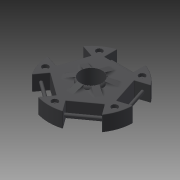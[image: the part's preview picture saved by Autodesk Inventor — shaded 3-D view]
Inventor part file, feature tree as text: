
AUTODESK INVENTOR PART (.ipt)
format: ipt  version: 2014 SP2 (Build 180246200, 246)  size: 1,258,496 bytes
history: native  units: mm
features: extrude x11, sketch x11, fillet x6, projected_geometry x3, pattern_circular x2
ambient origin geometry x8: Origin, YZ Plane, XZ Plane, XY Plane, X Axis, Y Axis, Z Axis, Center Point
bodies: Solid1 (feature_tree)
feature tree (33):
  extrude  "Extrusion1"  Depth=10.0mm TaperAngle=0.0deg
  extrude  "Extrusion2"  Depth=10.0mm TaperAngle=0.0deg
  extrude  "Extrusion3"  Depth=50.0mm TaperAngle=360.0deg
  extrude  "Extrusion4"  Depth=20.0mm TaperAngle=0.0deg
  pattern_circular  "Circular Pattern1"  Count=5 Angle=360.0deg
  extrude  "Extrusion5"  Depth=2.0mm TaperAngle=360.0deg
  extrude  "Extrusion6"  Depth=0.3mm
  extrude  "Extrusion7"  Depth=2.0mm
  fillet  "Fillet1"  Radius=2.5mm
  extrude  "Extrusion8"  Depth=2.0mm TaperAngle=0.0deg
  fillet  "Fillet2"  Radius=5.0mm
  fillet  "Fillet3"  Radius=2.0mm
  extrude  "Extrusion9"  Depth=2.0mm TaperAngle=360.0deg
  extrude  "Extrusion10"  [1 undecoded]
  fillet  "Fillet4"  [1 undecoded]
  fillet  "Fillet5"  [1 undecoded]
  fillet  "Fillet6"  [1 undecoded]
  pattern_circular  "Circular Pattern2"  [2 undecoded]
  extrude  "Extrusion11"  [1 undecoded]
  sketch  "Sketch1"  dims[d1=10.0mm d2=0.0mm d4=10.0mm d5=0.0mm]
  sketch  "Sketch2"  dims[d10=50.0mm d12=360.0deg d14=10.0mm d15=0.0mm]
  sketch  "Sketch3"  dims[d17=20.0mm d18=0.0mm d19=50.0mm d20=360.0deg]
  sketch  "Sketch4"  dims[d25=50.0mm d27=360.0deg d29=20.0mm d30=0.0mm d32=50.0mm d34=360.0deg]
  projected_geometry  "Projected Loop1"
  sketch  "Sketch5"  dims[d36=2.0mm d37=0.0mm d39=50.0mm d41=360.0deg]
  sketch  "Sketch6"  dims[d43=5.0mm d44=0.0mm d45=0.3mm]
  sketch  "Sketch7"  dims[d47=2.0mm d48=12.0mm d49=0.0mm d50=0.0mm d51=2.5mm d52=2.5mm]
  sketch  "Sketch8"  dims[d53=4.0mm d54=0.0mm d55=4.0mm d56=0.0mm d57=5.0mm d58=2.0mm]
  sketch  "Sketch9"  dims[d59=2.0mm d60=60.0mm d61=360.0deg]
  projected_geometry  "Projected Loop2"
  sketch  "Sketch10"  dims[d64=2.0mm d65=0.0mm]
  projected_geometry  "Projected Loop3"
  sketch  "Sketch11"
note: 7 required parameter values undecoded (feature->parameter linkage not recoverable at this tier; creation-order binding heuristic only, values carry confidence <= 0.55)
